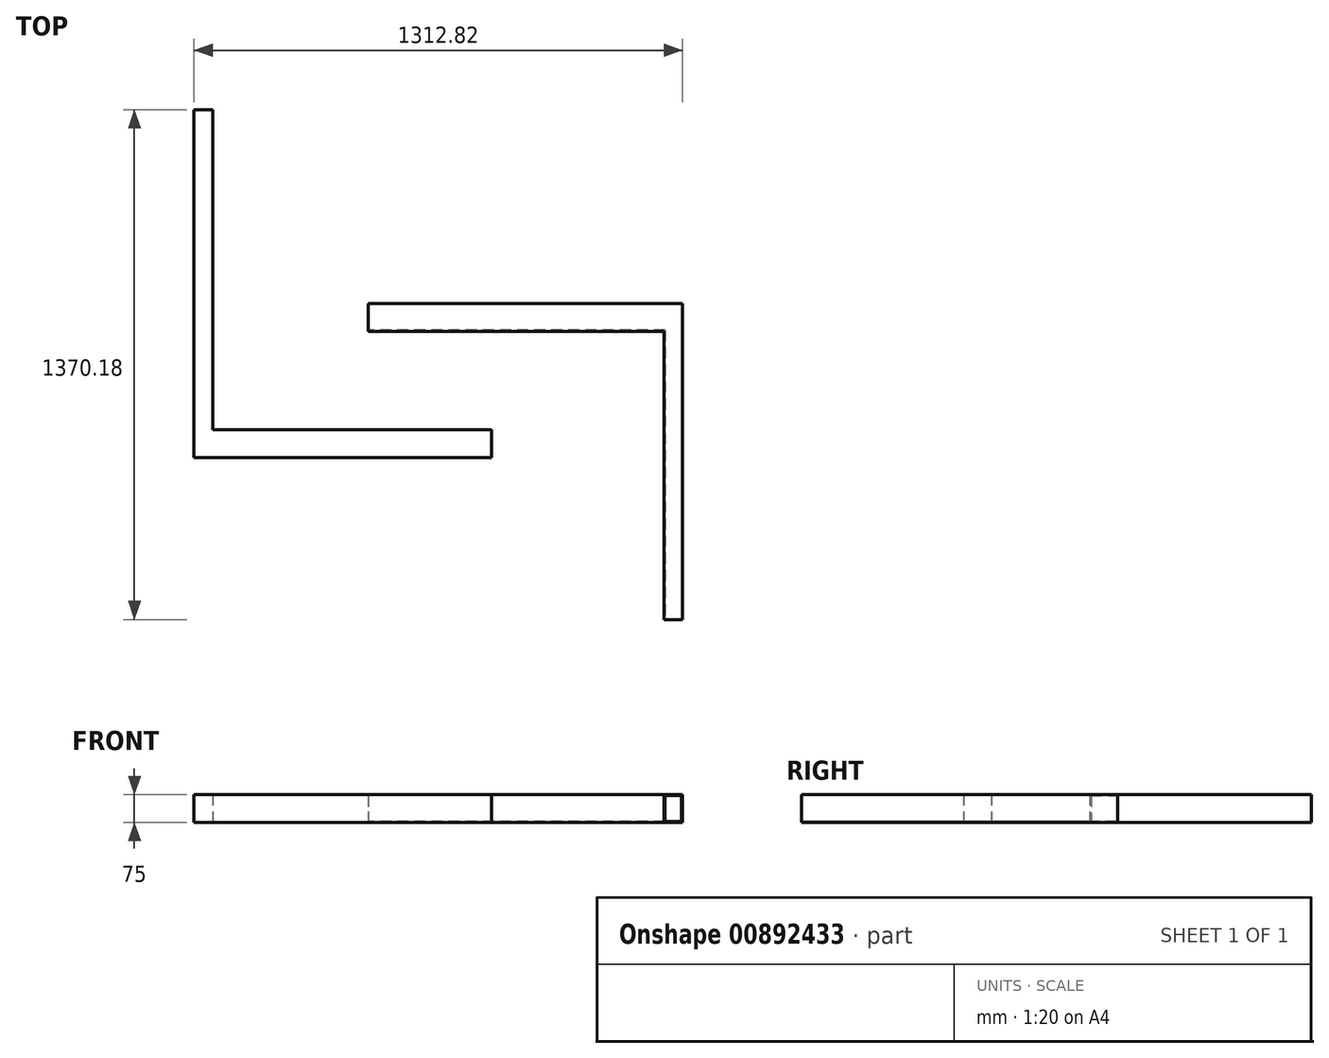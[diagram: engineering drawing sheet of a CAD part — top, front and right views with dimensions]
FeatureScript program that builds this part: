
annotation { "Feature Type Name" : "Feature", "Feature Type Description" : "" }
export const myFeature = defineFeature(function(context is Context, id is Id, definition is map)
    precondition{}
    {
        {
            var Q0;
            Q0=qCreatedBy(makeId("Top.planeOp"),FACE);
            var sketch = newSketch(context, id + "F0", { "sketchPlane" : qUnion([Q0])});
            skLineSegment(sketch, "E0.bottom", {"start": v(0, 0) * mm, "end": v(750, 0) * mm});
            skLineSegment(sketch, "E0.top", {"start": v(0, -75) * mm, "end": v(750, -75) * mm});
            skLineSegment(sketch, "E0.left", {"start": v(0, 0) * mm, "end": v(0, -75) * mm});
            skLineSegment(sketch, "E0.right", {"start": v(750, 0) * mm, "end": v(750, -75) * mm});
            skLineSegment(sketch, "E1.bottom", {"start": v(0, 0) * mm, "end": v(-50, 0) * mm});
            skLineSegment(sketch, "E1.top", {"start": v(0, 860) * mm, "end": v(-50, 860) * mm});
            skLineSegment(sketch, "E1.left", {"start": v(0, 0) * mm, "end": v(0, 860) * mm});
            skLineSegment(sketch, "E1.right", {"start": v(-50, 0) * mm, "end": v(-50, 860) * mm});
            skLineSegment(sketch, "E2.top", {"start": v(0, -75) * mm, "end": v(-50, -75) * mm});
            skLineSegment(sketch, "E2.right", {"start": v(-50, 0) * mm, "end": v(-50, -75) * mm});
            skLineSegment(sketch, "E3.bottom", {"start": v(1212.82, 264.82) * mm, "end": v(417.82, 264.82) * mm});
            skLineSegment(sketch, "E3.top", {"start": v(1212.82, 339.82) * mm, "end": v(417.82, 339.82) * mm});
            skLineSegment(sketch, "E3.left", {"start": v(1212.82, 264.82) * mm, "end": v(1212.82, 339.82) * mm});
            skLineSegment(sketch, "E3.right", {"start": v(417.82, 264.82) * mm, "end": v(417.82, 339.82) * mm});
            skLineSegment(sketch, "E4.bottom", {"start": v(1212.82, 264.82) * mm, "end": v(1262.82, 264.82) * mm});
            skLineSegment(sketch, "E4.top", {"start": v(1212.82, -510.18) * mm, "end": v(1262.82, -510.18) * mm});
            skLineSegment(sketch, "E4.left", {"start": v(1212.82, 264.82) * mm, "end": v(1212.82, -510.18) * mm});
            skLineSegment(sketch, "E4.right", {"start": v(1262.82, 264.82) * mm, "end": v(1262.82, -510.18) * mm});
            skLineSegment(sketch, "E5.bottom", {"start": v(1262.82, 264.82) * mm, "end": v(1212.82, 264.82) * mm});
            skLineSegment(sketch, "E5.top", {"start": v(1262.82, 339.82) * mm, "end": v(1212.82, 339.82) * mm});
            skLineSegment(sketch, "E5.left", {"start": v(1262.82, 264.82) * mm, "end": v(1262.82, 339.82) * mm});
            skSolve(sketch);
        }
        {
            var Q0;
            Q0=makeQuery(id+"F0.imprint","IMPRINT",FACE,{"disambiguationData":[TD([[makeQuery(id+"F0.imprint","IMPRINT",EDGE,{"derivedFrom":sQuery(id+"F0.wireOp",EDGE,"E0.bottom")}),-1.0]])]});
            var Q1;
            Q1=makeQuery(id+"F0.imprint","IMPRINT",FACE,{"disambiguationData":[TD([[makeQuery(id+"F0.imprint","IMPRINT",EDGE,{"derivedFrom":sQuery(id+"F0.wireOp",EDGE,"E1.top")}),1.0]])]});
            var Q2;
            Q2=makeQuery(id+"F0.imprint","IMPRINT",FACE,{"disambiguationData":[TD([[makeQuery(id+"F0.imprint","IMPRINT",EDGE,{"derivedFrom":sQuery(id+"F0.wireOp",EDGE,"E1.bottom")}),1.0]])]});
            var Q3;
            Q3=sQuery(id+"F0.wireOp",EDGE,"E1.right");
            var Q4;
            Q4=sQuery(id+"F0.wireOp",EDGE,"E2.right");
            var Q5;
            Q5=sQuery(id+"F0.wireOp",EDGE,"E2.top");
            var Q6;
            Q6=sQuery(id+"F0.wireOp",EDGE,"E0.bottom");
            var Q7;
            Q7=sQuery(id+"F0.wireOp",EDGE,"E0.top");
            var Q8;
            Q8=sQuery(id+"F0.wireOp",EDGE,"E0.right");
            var Q9;
            Q9=sQuery(id+"F0.wireOp",EDGE,"E1.left");
            var Q10;
            Q10=sQuery(id+"F0.wireOp",EDGE,"E1.top");
            extrude(context, id + "F1", {"entities" : qUnion([Q0, Q1, Q2]), "surfaceEntities" : qUnion([Q3, Q4, Q5, Q6, Q7, Q8, Q9, Q10]), "depth" : 75 * mm, "offsetDistance" : 25 * mm});
        }
        {
            var Q0;
            Q0=makeQuery(id+"F1.opExtrude","SWEPT_FACE",FACE,{"disambiguationData":[OSD([sQuery(id+"F0.wireOp",EDGE,"E0.right")])]});
            var Q1;
            Q1=makeQuery(id+"F1.opExtrude","SWEPT_FACE",FACE,{"disambiguationData":[OSD([sQuery(id+"F0.wireOp",EDGE,"E1.top")])]});
            shell(context, id + "F2", {"entities" : qUnion([Q0, Q1]), "thickness" : 3 * mm});
        }
        {
            var Q0;
            Q0 = qSketchRegion(id + "F0", true);
            extrude(context, id + "F3", {"entities" : qUnion([Q0]), "operationType" : NewBodyOperationType.ADD, "depth" : 75 * mm, "offsetDistance" : 25 * mm});
        }
        {
            var Q0;
            Q0=makeQuery(id+"F3.opExtrude","SWEPT_FACE",FACE,{"disambiguationData":[OSD([sQuery(id+"F0.wireOp",EDGE,"E3.right")])]});
            var Q1;
            Q1=makeQuery(id+"F3.opExtrude","SWEPT_FACE",FACE,{"disambiguationData":[OSD([sQuery(id+"F0.wireOp",EDGE,"E4.top")])]});
            shell(context, id + "F4", {"entities" : qUnion([Q0, Q1]), "thickness" : 3 * mm});
        }
    });
